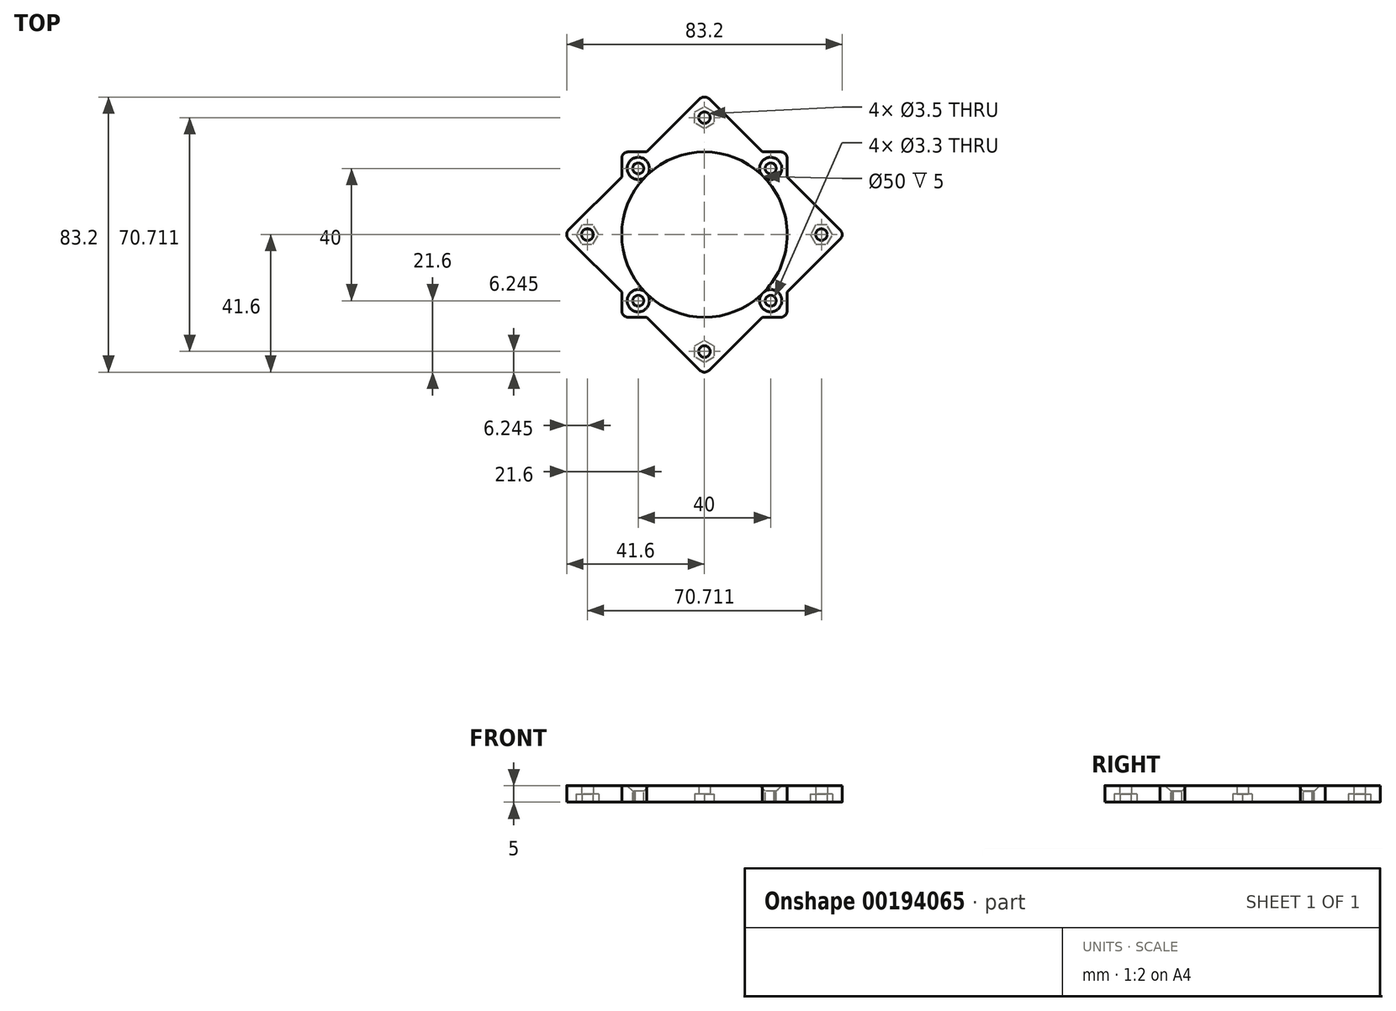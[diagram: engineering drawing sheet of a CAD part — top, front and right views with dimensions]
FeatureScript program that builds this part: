
annotation { "Feature Type Name" : "Feature", "Feature Type Description" : "" }
export const myFeature = defineFeature(function(context is Context, id is Id, definition is map)
    precondition{}
    {
        {
            assignVariable(context, id + "F0", {"name" : "plate_thickness", "anyValue" : 5});
        }
        {
            var Q0;
            Q0=qCreatedBy(makeId("Top.planeOp"),FACE);
            var sketch = newSketch(context, id + "F1", { "sketchPlane" : qUnion([Q0])});
            skLineSegment(sketch, "E0.bottom", {"start": v(-41.01, 1.41) * mm, "end": v(-1.41, 41.01) * mm});
            skLineSegment(sketch, "E0.top", {"start": v(1.41, -41.01) * mm, "end": v(41.01, -1.41) * mm});
            skLineSegment(sketch, "E0.left", {"start": v(-41.01, -1.41) * mm, "end": v(-1.41, -41.01) * mm});
            skLineSegment(sketch, "E0.right", {"start": v(1.41, 41.01) * mm, "end": v(41.01, 1.41) * mm});
            skPoint(sketch, "E0.middle", {"position": v(0, 0) * mm});
            skPoint(sketch, "E1.endSnap0", {"position": v(-21.21, 21.21) * mm});
            skPoint(sketch, "E2.endSnap0", {"position": v(21.21, 21.21) * mm});
            skCircle(sketch, "E3", {"center": v(0, -35.36) * mm, "radius": 1.75 * mm});
            skLineSegment(sketch, "E4", {"start": v(0, -42.43) * mm, "end": v(0, 42.43) * mm, "construction": true});
            skLineSegment(sketch, "E5", {"start": v(-42.43, 0) * mm, "end": v(42.43, 0) * mm, "construction": true});
            skPoint(sketch, "E6.visualSharp", {"position": v(0, -42.43) * mm});
            skArc(sketch, "E7.filletArc", {"start": v(-1.41, -41.01) * mm, "mid": v(0, -41.6) * mm, "end": v(1.41, -41.01) * mm});
            skPoint(sketch, "E8.visualSharp", {"position": v(42.43, 0) * mm});
            skArc(sketch, "E8.filletArc", {"start": v(41.01, -1.41) * mm, "mid": v(41.6, 0) * mm, "end": v(41.01, 1.41) * mm});
            skPoint(sketch, "E9.visualSharp", {"position": v(0, 42.43) * mm});
            skArc(sketch, "E9.filletArc", {"start": v(1.41, 41.01) * mm, "mid": v(0, 41.6) * mm, "end": v(-1.41, 41.01) * mm});
            skPoint(sketch, "E10.visualSharp", {"position": v(-42.43, 0) * mm});
            skArc(sketch, "E10.filletArc", {"start": v(-41.01, 1.41) * mm, "mid": v(-41.6, 0) * mm, "end": v(-41.01, -1.41) * mm});
            skLineSegment(sketch, "E11", {"start": v(21.21, -21.21) * mm, "end": v(-21.21, 21.21) * mm, "construction": true});
            skLineSegment(sketch, "E12", {"start": v(21.21, 21.21) * mm, "end": v(-21.21, -21.21) * mm, "construction": true});
            skCircle(sketch, "E13.MirrorC", {"center": v(-35.36, 0) * mm, "radius": 1.75 * mm});
            skCircle(sketch, "E14.MirrorC", {"center": v(0, 35.36) * mm, "radius": 1.75 * mm});
            skCircle(sketch, "E15.MirrorC", {"center": v(35.36, 0) * mm, "radius": 1.75 * mm});
            skLineSegment(sketch, "E16", {"start": v(0, -35.36) * mm, "end": v(-3.54, -38.9) * mm, "construction": true});
            skSolve(sketch);
        }
        {
            var Q0;
            Q0=makeQuery(id+"F1.imprint","IMPRINT",FACE,{"disambiguationData":[TD([[makeQuery(id+"F1.imprint","IMPRINT",EDGE,{"derivedFrom":sQuery(id+"F1.wireOp",EDGE,"E0.bottom")}),-1.0]])]});
            extrude(context, id + "F2", {"entities" : qUnion([Q0]), "depth" : getVariable(context, 'plate_thickness') * mm});
        }
        {
            var Q0;
            Q0=qCreatedBy(makeId("Top.planeOp"),FACE);
            var sketch = newSketch(context, id + "F3", { "sketchPlane" : qUnion([Q0])});
            skLineSegment(sketch, "E17.bottom", {"start": v(-23, 25) * mm, "end": v(23, 25) * mm});
            skLineSegment(sketch, "E17.top", {"start": v(-23, -25) * mm, "end": v(23, -25) * mm});
            skLineSegment(sketch, "E17.left", {"start": v(-25, 23) * mm, "end": v(-25, -23) * mm});
            skLineSegment(sketch, "E17.right", {"start": v(25, 23) * mm, "end": v(25, -23) * mm});
            skPoint(sketch, "E17.middle", {"position": v(0, 0) * mm});
            skPoint(sketch, "E18.endSnap0", {"position": v(0, 25) * mm});
            skPoint(sketch, "E19.endSnap0", {"position": v(25, 0) * mm});
            skCircle(sketch, "E20", {"center": v(-20, -20) * mm, "radius": 1.75 * mm});
            skLineSegment(sketch, "E21", {"start": v(-25, -25) * mm, "end": v(25, 25) * mm, "construction": true});
            skLineSegment(sketch, "E22", {"start": v(-25, 25) * mm, "end": v(25, -25) * mm, "construction": true});
            skPoint(sketch, "E23.visualSharp", {"position": v(-25, -25) * mm});
            skArc(sketch, "E24.filletArc", {"start": v(-25, -23) * mm, "mid": v(-24.41, -24.41) * mm, "end": v(-23, -25) * mm});
            skPoint(sketch, "E25.visualSharp", {"position": v(25, -25) * mm});
            skArc(sketch, "E25.filletArc", {"start": v(23, -25) * mm, "mid": v(24.41, -24.41) * mm, "end": v(25, -23) * mm});
            skPoint(sketch, "E26.visualSharp", {"position": v(25, 25) * mm});
            skArc(sketch, "E26.filletArc", {"start": v(25, 23) * mm, "mid": v(24.41, 24.41) * mm, "end": v(23, 25) * mm});
            skPoint(sketch, "E27.visualSharp", {"position": v(-25, 25) * mm});
            skArc(sketch, "E27.filletArc", {"start": v(-23, 25) * mm, "mid": v(-24.41, 24.41) * mm, "end": v(-25, 23) * mm});
            skCircle(sketch, "E28.MirrorC", {"center": v(20, -20) * mm, "radius": 1.75 * mm});
            skCircle(sketch, "E29.MirrorC", {"center": v(20, 20) * mm, "radius": 1.75 * mm});
            skCircle(sketch, "E30.MirrorC", {"center": v(-20, 20) * mm, "radius": 1.75 * mm});
            skSolve(sketch);
        }
        {
            var Q0;
            Q0 = qSketchRegion(id + "F3", true);
            extrude(context, id + "F4", {"entities" : qUnion([Q0]), "depth" : getVariable(context, 'plate_thickness') * mm});
        }
        {
            var Q0;
            Q0=makeQuery(id+"F4.opExtrude","SWEPT_BODY",BODY,{"disambiguationData":[OSD([sQuery(id+"F3.wireOp",EDGE,"E17.bottom"),sQuery(id+"F3.wireOp",EDGE,"E17.top"),sQuery(id+"F3.wireOp",EDGE,"E17.left"),sQuery(id+"F3.wireOp",EDGE,"E17.right"),sQuery(id+"F3.wireOp",EDGE,"E20"),sQuery(id+"F3.wireOp",EDGE,"56bc1b40-8556-4916-879a-06b11f969edb"),sQuery(id+"F3.wireOp",EDGE,"E24.filletArc"),sQuery(id+"F3.wireOp",EDGE,"E25.filletArc"),sQuery(id+"F3.wireOp",EDGE,"E26.filletArc"),sQuery(id+"F3.wireOp",EDGE,"E27.filletArc"),sQuery(id+"F3.wireOp",EDGE,"E28.MirrorC"),sQuery(id+"F3.wireOp",EDGE,"E29.MirrorC"),sQuery(id+"F3.wireOp",EDGE,"E30.MirrorC")])]});
            var Q1;
            Q1=makeQuery(id+"F2.opExtrude","SWEPT_BODY",BODY,{"disambiguationData":[OSD([sQuery(id+"F1.wireOp",EDGE,"E0.bottom"),sQuery(id+"F1.wireOp",EDGE,"E0.top"),sQuery(id+"F1.wireOp",EDGE,"E0.left"),sQuery(id+"F1.wireOp",EDGE,"E0.right"),sQuery(id+"F1.wireOp",EDGE,"E3"),sQuery(id+"F1.wireOp",EDGE,"ej8KbIMe-PWYS-cAjW-iybb-MyuX8oysgDMn"),sQuery(id+"F1.wireOp",EDGE,"E7.filletArc"),sQuery(id+"F1.wireOp",EDGE,"E8.filletArc"),sQuery(id+"F1.wireOp",EDGE,"E9.filletArc"),sQuery(id+"F1.wireOp",EDGE,"E10.filletArc"),sQuery(id+"F1.wireOp",EDGE,"1b3d5ee1-3fd6-4c55-bd02-d0c0132213120.MirrorC"),sQuery(id+"F1.wireOp",EDGE,"01bf5ec6-f76a-4ebe-8428-037c4d78945e0.MirrorC"),sQuery(id+"F1.wireOp",EDGE,"01bf5ec6-f76a-4ebe-8428-037c4d78945e1.MirrorC")])]});
            booleanBodies(context, id + "F5", {"operationType" : BooleanOperationType.UNION, "tools" : qUnion([Q0, Q1])});
        }
        {
            var Q0;
            Q0=makeQuery(id+"F5.opBoolean","MERGE",FACE,{"derivedFrom":[makeQuery(id+"F2.opExtrude","CAP_FACE",FACE,{"disambiguationData":[OSD([sQuery(id+"F1.wireOp",EDGE,"E0.bottom"),sQuery(id+"F1.wireOp",EDGE,"E0.top"),sQuery(id+"F1.wireOp",EDGE,"E0.left"),sQuery(id+"F1.wireOp",EDGE,"E0.right"),sQuery(id+"F1.wireOp",EDGE,"E3"),sQuery(id+"F1.wireOp",EDGE,"E7.filletArc"),sQuery(id+"F1.wireOp",EDGE,"E8.filletArc"),sQuery(id+"F1.wireOp",EDGE,"E9.filletArc"),sQuery(id+"F1.wireOp",EDGE,"E10.filletArc"),sQuery(id+"F1.wireOp",EDGE,"E13.MirrorC"),sQuery(id+"F1.wireOp",EDGE,"E14.MirrorC"),sQuery(id+"F1.wireOp",EDGE,"E15.MirrorC")])],"isStart":false}),makeQuery(id+"F4.opExtrude","CAP_FACE",FACE,{"disambiguationData":[OSD([sQuery(id+"F3.wireOp",EDGE,"E17.bottom"),sQuery(id+"F3.wireOp",EDGE,"E17.top"),sQuery(id+"F3.wireOp",EDGE,"E17.left"),sQuery(id+"F3.wireOp",EDGE,"E17.right"),sQuery(id+"F3.wireOp",EDGE,"E20"),sQuery(id+"F3.wireOp",EDGE,"E24.filletArc"),sQuery(id+"F3.wireOp",EDGE,"E25.filletArc"),sQuery(id+"F3.wireOp",EDGE,"E26.filletArc"),sQuery(id+"F3.wireOp",EDGE,"E27.filletArc"),sQuery(id+"F3.wireOp",EDGE,"E28.MirrorC"),sQuery(id+"F3.wireOp",EDGE,"E29.MirrorC"),sQuery(id+"F3.wireOp",EDGE,"E30.MirrorC")])],"isStart":false})]});
            var sketch = newSketch(context, id + "F6", { "sketchPlane" : qUnion([Q0])});
            skCircle(sketch, "E31", {"center": v(0, 0) * mm, "radius": 25 * mm});
            skSolve(sketch);
        }
        {
            var Q0;
            Q0=makeQuery(id+"F6.imprint","IMPRINT",FACE,{"disambiguationData":[TD([[makeQuery(id+"F6.imprint","IMPRINT",EDGE,{"derivedFrom":sQuery(id+"F6.wireOp",EDGE,"E31")}),1.0]])]});
            extrude(context, id + "F7", {"entities" : qUnion([Q0]), "operationType" : NewBodyOperationType.REMOVE, "endBound" : BoundingType.THROUGH_ALL, "oppositeDirection" : true, "depth" : 25 * mm});
        }
        {
            var Q0;
            Q0=makeQuery(id+"F4.opExtrude","SWEPT_BODY",BODY,{"disambiguationData":[OSD([sQuery(id+"F3.wireOp",EDGE,"E17.bottom"),sQuery(id+"F3.wireOp",EDGE,"E17.top"),sQuery(id+"F3.wireOp",EDGE,"E17.left"),sQuery(id+"F3.wireOp",EDGE,"E17.right"),sQuery(id+"F3.wireOp",EDGE,"E20"),sQuery(id+"F3.wireOp",EDGE,"56bc1b40-8556-4916-879a-06b11f969edb"),sQuery(id+"F3.wireOp",EDGE,"E24.filletArc"),sQuery(id+"F3.wireOp",EDGE,"E25.filletArc"),sQuery(id+"F3.wireOp",EDGE,"E26.filletArc"),sQuery(id+"F3.wireOp",EDGE,"E27.filletArc"),sQuery(id+"F3.wireOp",EDGE,"E28.MirrorC"),sQuery(id+"F3.wireOp",EDGE,"E29.MirrorC"),sQuery(id+"F3.wireOp",EDGE,"E30.MirrorC")])]});
            transform(context, id + "F8", {"entities" : qUnion([Q0]), "transformType" : TransformType.TRANSLATION_3D, "dx" : 0 * mm, "dy" : 0 * mm, "dz" : -5 * mm, "makeCopy" : false});
        }
        {
            var Q0;
            Q0=sQuery(id+"F3.wireOp",VERTEX,"E20.center");
            var Q1;
            Q1=sQuery(id+"F3.wireOp",VERTEX,"E29.MirrorC.center");
            var Q2;
            Q2=sQuery(id+"F3.wireOp",VERTEX,"E28.MirrorC.center");
            var Q3;
            Q3=sQuery(id+"F3.wireOp",VERTEX,"E30.MirrorC.center");
            var Q4;
            Q4=makeQuery(id+"F4.opExtrude","SWEPT_BODY",BODY,{"disambiguationData":[OSD([sQuery(id+"F3.wireOp",EDGE,"E17.bottom"),sQuery(id+"F3.wireOp",EDGE,"E17.top"),sQuery(id+"F3.wireOp",EDGE,"E17.left"),sQuery(id+"F3.wireOp",EDGE,"E17.right"),sQuery(id+"F3.wireOp",EDGE,"E20"),sQuery(id+"F3.wireOp",EDGE,"56bc1b40-8556-4916-879a-06b11f969edb"),sQuery(id+"F3.wireOp",EDGE,"E24.filletArc"),sQuery(id+"F3.wireOp",EDGE,"E25.filletArc"),sQuery(id+"F3.wireOp",EDGE,"E26.filletArc"),sQuery(id+"F3.wireOp",EDGE,"E27.filletArc"),sQuery(id+"F3.wireOp",EDGE,"E28.MirrorC"),sQuery(id+"F3.wireOp",EDGE,"E29.MirrorC"),sQuery(id+"F3.wireOp",EDGE,"E30.MirrorC")])]});
            hole(context, id + "F9", {"style" : HoleStyle.C_SINK, "endStyle" : HoleEndStyle.THROUGH, "standardTappedOrClearance" : lookupTablePath({ "standard" : "ISO", "fit" : "Normal", "size" : "M3", "type" : "Clearance" }), "standardBlindInLast" : lookupTablePath({ "fit" : "Standard", "standard" : "ISO", "size" : "M3", "type" : "Clearance" }), "holeDiameter" : 3.3 * mm, "cSinkDiameter" : 6.72 * mm, "cSinkAngle" : 90 * degree, "locations" : qUnion([Q0, Q1, Q2, Q3]), "scope" : qUnion([Q4]), "isTappedThrough" : true});
        }
        {
            var Q0;
            Q0=makeQuery(id+"F5.opBoolean","MERGE",FACE,{"derivedFrom":[makeQuery(id+"F2.opExtrude","CAP_FACE",FACE,{"disambiguationData":[OSD([sQuery(id+"F1.wireOp",EDGE,"E0.bottom"),sQuery(id+"F1.wireOp",EDGE,"E0.top"),sQuery(id+"F1.wireOp",EDGE,"E0.left"),sQuery(id+"F1.wireOp",EDGE,"E0.right"),sQuery(id+"F1.wireOp",EDGE,"E3"),sQuery(id+"F1.wireOp",EDGE,"ej8KbIMe-PWYS-cAjW-iybb-MyuX8oysgDMn"),sQuery(id+"F1.wireOp",EDGE,"E7.filletArc"),sQuery(id+"F1.wireOp",EDGE,"E8.filletArc"),sQuery(id+"F1.wireOp",EDGE,"E9.filletArc"),sQuery(id+"F1.wireOp",EDGE,"E10.filletArc"),sQuery(id+"F1.wireOp",EDGE,"1b3d5ee1-3fd6-4c55-bd02-d0c0132213120.MirrorC"),sQuery(id+"F1.wireOp",EDGE,"01bf5ec6-f76a-4ebe-8428-037c4d78945e0.MirrorC"),sQuery(id+"F1.wireOp",EDGE,"01bf5ec6-f76a-4ebe-8428-037c4d78945e1.MirrorC")])],"isStart":true}),makeQuery(id+"F4.opExtrude","CAP_FACE",FACE,{"disambiguationData":[OSD([sQuery(id+"F3.wireOp",EDGE,"E17.bottom"),sQuery(id+"F3.wireOp",EDGE,"E17.top"),sQuery(id+"F3.wireOp",EDGE,"E17.left"),sQuery(id+"F3.wireOp",EDGE,"E17.right"),sQuery(id+"F3.wireOp",EDGE,"E20"),sQuery(id+"F3.wireOp",EDGE,"56bc1b40-8556-4916-879a-06b11f969edb"),sQuery(id+"F3.wireOp",EDGE,"E24.filletArc"),sQuery(id+"F3.wireOp",EDGE,"E25.filletArc"),sQuery(id+"F3.wireOp",EDGE,"E26.filletArc"),sQuery(id+"F3.wireOp",EDGE,"E27.filletArc"),sQuery(id+"F3.wireOp",EDGE,"E28.MirrorC"),sQuery(id+"F3.wireOp",EDGE,"E29.MirrorC"),sQuery(id+"F3.wireOp",EDGE,"E30.MirrorC")])],"isStart":true})]});
            var sketch = newSketch(context, id + "F10", { "sketchPlane" : qUnion([Q0])});
            skCircle(sketch, "E32.cCircle", {"center": v(35.36, 0) * mm, "radius": 3.38 * mm, "construction": true});
            skLineSegment(sketch, "E32.0", {"start": v(33.67, 2.92) * mm, "end": v(37.04, 2.92) * mm});
            skLineSegment(sketch, "E32.1", {"start": v(37.04, 2.92) * mm, "end": v(38.73, 0) * mm});
            skLineSegment(sketch, "E32.2", {"start": v(38.73, 0) * mm, "end": v(37.04, -2.92) * mm});
            skLineSegment(sketch, "E32.3", {"start": v(37.04, -2.92) * mm, "end": v(33.67, -2.92) * mm});
            skLineSegment(sketch, "E32.4", {"start": v(33.67, -2.92) * mm, "end": v(31.98, 0) * mm});
            skLineSegment(sketch, "E32.5", {"start": v(31.98, 0) * mm, "end": v(33.67, 2.92) * mm});
            skLineSegment(sketch, "E33.MirrorCS", {"start": v(2.92, -37.04) * mm, "end": v(2.92, -33.67) * mm});
            skCircle(sketch, "E34.MirrorC", {"center": v(0, -35.36) * mm, "radius": 3.38 * mm, "construction": true});
            skLineSegment(sketch, "E35.MirrorCS", {"start": v(-2.92, -33.67) * mm, "end": v(-2.92, -37.04) * mm});
            skLineSegment(sketch, "E36.MirrorCS", {"start": v(-2.92, -37.04) * mm, "end": v(0, -38.73) * mm});
            skLineSegment(sketch, "E37.MirrorCS", {"start": v(0, -38.73) * mm, "end": v(2.92, -37.04) * mm});
            skLineSegment(sketch, "E38.MirrorCS", {"start": v(2.92, -33.67) * mm, "end": v(0, -31.98) * mm});
            skLineSegment(sketch, "E39.MirrorCS", {"start": v(0, -31.98) * mm, "end": v(-2.92, -33.67) * mm});
            skLineSegment(sketch, "E40.MirrorCS", {"start": v(-37.04, -2.92) * mm, "end": v(-38.73, 0) * mm});
            skLineSegment(sketch, "E41.MirrorCS", {"start": v(-37.04, 2.92) * mm, "end": v(-33.67, 2.92) * mm});
            skLineSegment(sketch, "E42.MirrorCS", {"start": v(0, 31.98) * mm, "end": v(2.92, 33.67) * mm});
            skLineSegment(sketch, "E43.MirrorCS", {"start": v(2.92, 33.67) * mm, "end": v(2.92, 37.04) * mm});
            skLineSegment(sketch, "E44.MirrorCS", {"start": v(-31.98, 0) * mm, "end": v(-33.67, -2.92) * mm});
            skLineSegment(sketch, "E45.MirrorCS", {"start": v(0, 38.73) * mm, "end": v(-2.92, 37.04) * mm});
            skLineSegment(sketch, "E46.MirrorCS", {"start": v(-38.73, 0) * mm, "end": v(-37.04, 2.92) * mm});
            skLineSegment(sketch, "E47.MirrorCS", {"start": v(2.92, 37.04) * mm, "end": v(0, 38.73) * mm});
            skLineSegment(sketch, "E48.MirrorCS", {"start": v(-2.92, 37.04) * mm, "end": v(-2.92, 33.67) * mm});
            skLineSegment(sketch, "E49.MirrorCS", {"start": v(-33.67, 2.92) * mm, "end": v(-31.98, 0) * mm});
            skCircle(sketch, "E50.MirrorC", {"center": v(-35.36, 0) * mm, "radius": 3.38 * mm, "construction": true});
            skCircle(sketch, "E51.MirrorC", {"center": v(0, 35.36) * mm, "radius": 3.38 * mm, "construction": true});
            skLineSegment(sketch, "E52.MirrorCS", {"start": v(-2.92, 33.67) * mm, "end": v(0, 31.98) * mm});
            skLineSegment(sketch, "E53.MirrorCS", {"start": v(-33.67, -2.92) * mm, "end": v(-37.04, -2.92) * mm});
            skSolve(sketch);
        }
        {
            var Q0;
            {var subQ14=sQuery(id+"F10.wireOp",EDGE,"E32.0");Q0=makeQuery(id+"F10.imprint","IMPRINT",FACE,{"disambiguationData":[TD([[makeQuery(id+"F10.imprint","IMPRINT",EDGE,{"derivedFrom":subQ14}),-1.0]])]});}
            var Q1;
            Q1=makeQuery(id+"F10.imprint","IMPRINT",FACE,{"disambiguationData":[TD([[makeQuery(id+"F10.imprint","IMPRINT",EDGE,{"derivedFrom":sQuery(id+"F10.wireOp",EDGE,"E42.MirrorCS")}),1.0]])]});
            var Q2;
            {var subQ21=sQuery(id+"F10.wireOp",EDGE,"E35.MirrorCS");Q2=makeQuery(id+"F10.imprint","IMPRINT",FACE,{"disambiguationData":[TD([[makeQuery(id+"F10.imprint","IMPRINT",EDGE,{"derivedFrom":subQ21}),1.0]])]});}
            var Q3;
            Q3=makeQuery(id+"F10.imprint","IMPRINT",FACE,{"disambiguationData":[TD([[makeQuery(id+"F10.imprint","IMPRINT",EDGE,{"derivedFrom":sQuery(id+"F10.wireOp",EDGE,"E44.MirrorCS")}),-1.0]])]});
            extrude(context, id + "F11", {"entities" : qUnion([Q0, Q1, Q2, Q3]), "operationType" : NewBodyOperationType.REMOVE, "oppositeDirection" : true, "depth" : 2.5 * mm});
        }
    });
